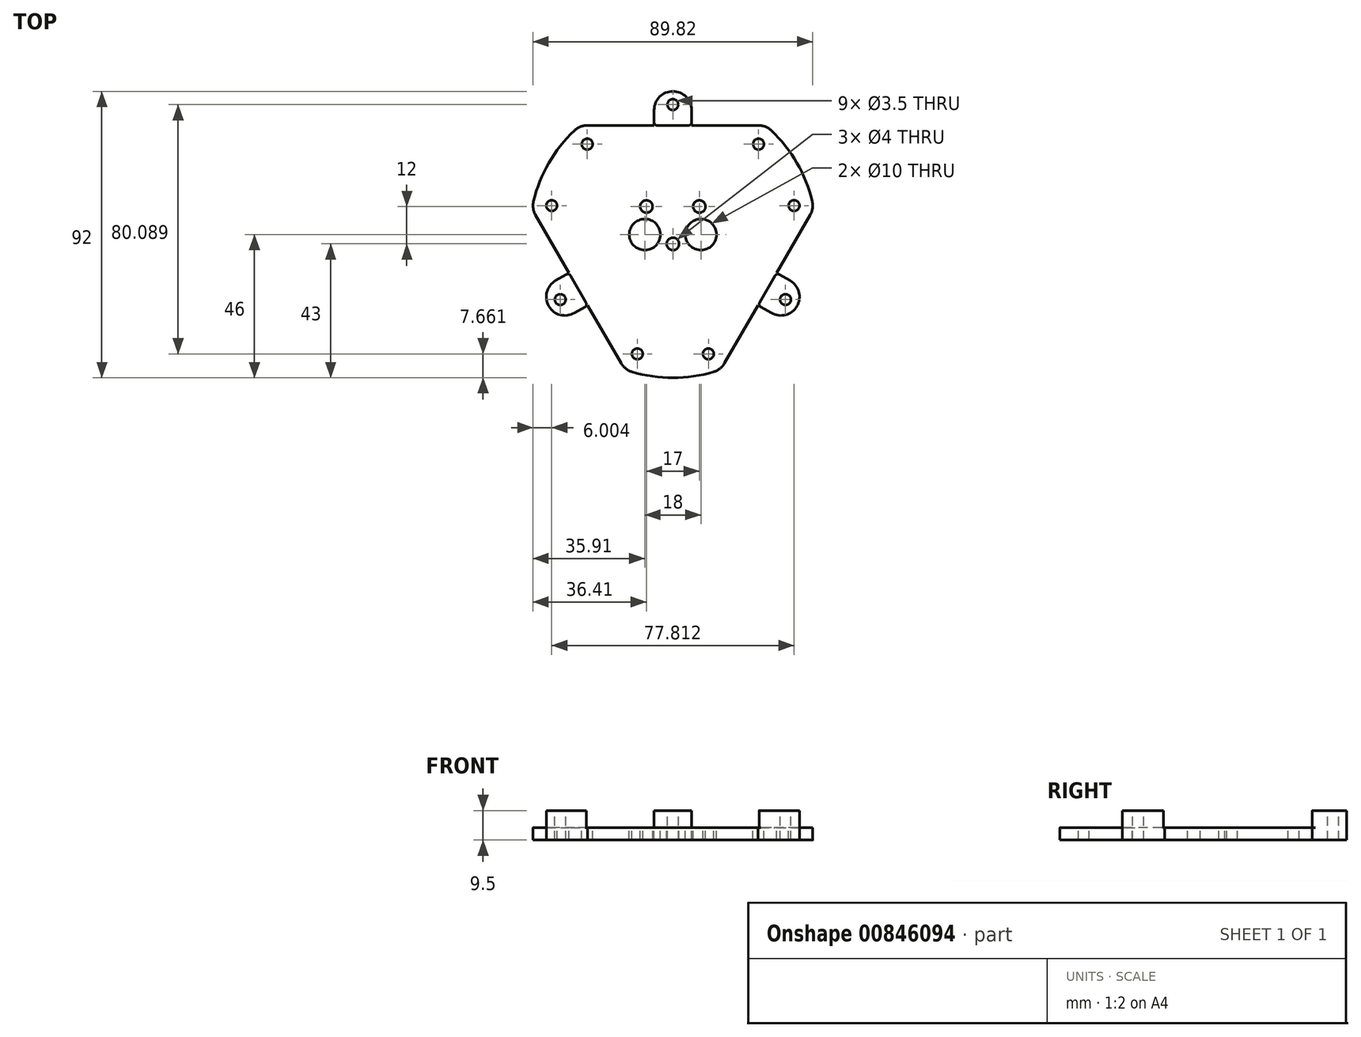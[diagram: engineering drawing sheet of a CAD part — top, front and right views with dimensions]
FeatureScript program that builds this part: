
annotation { "Feature Type Name" : "Feature", "Feature Type Description" : "" }
export const myFeature = defineFeature(function(context is Context, id is Id, definition is map)
    precondition{}
    {
        {
            var Q0;
            Q0=qCreatedBy(makeId("Top.planeOp"),FACE);
            var sketch = newSketch(context, id + "F0", { "sketchPlane" : qUnion([Q0])});
            skCircle(sketch, "E0", {"center": v(-38.9, 9.3) * mm, "radius": 1.75 * mm});
            skCircle(sketch, "E1", {"center": v(-38.9, 9.3) * mm, "radius": 6 * mm});
            skCircle(sketch, "E2", {"center": v(-11.4, -38.34) * mm, "radius": 1.75 * mm});
            skCircle(sketch, "E3", {"center": v(-11.4, -38.34) * mm, "radius": 6 * mm});
            skCircle(sketch, "E4", {"center": v(11.4, -38.34) * mm, "radius": 6 * mm});
            skCircle(sketch, "E5", {"center": v(11.4, -38.34) * mm, "radius": 1.75 * mm});
            skCircle(sketch, "E6", {"center": v(38.9, 9.3) * mm, "radius": 1.75 * mm});
            skCircle(sketch, "E7", {"center": v(38.9, 9.3) * mm, "radius": 6 * mm});
            skCircle(sketch, "E8", {"center": v(-27.5, 29.05) * mm, "radius": 1.75 * mm});
            skCircle(sketch, "E9", {"center": v(-27.5, 29.05) * mm, "radius": 6 * mm});
            skCircle(sketch, "E10", {"center": v(27.5, 29.05) * mm, "radius": 1.75 * mm});
            skCircle(sketch, "E11", {"center": v(27.5, 29.05) * mm, "radius": 6 * mm});
            skLineSegment(sketch, "E12", {"start": v(-27.5, 29.05) * mm, "end": v(27.5, 29.05) * mm, "construction": true});
            skLineSegment(sketch, "E13", {"start": v(38.9, 9.3) * mm, "end": v(11.4, -38.34) * mm, "construction": true});
            skLineSegment(sketch, "E14", {"start": v(-11.4, -38.34) * mm, "end": v(-38.9, 9.3) * mm, "construction": true});
            skCircle(sketch, "E15", {"center": v(0, 0) * mm, "radius": 40 * mm, "construction": true});
            skCircle(sketch, "E16", {"center": v(0, 0) * mm, "radius": 46 * mm});
            skLineSegment(sketch, "E17", {"start": v(-44.1, 6.3) * mm, "end": v(-16.6, -41.34) * mm});
            skLineSegment(sketch, "E18", {"start": v(16.6, -41.34) * mm, "end": v(44.1, 6.3) * mm});
            skLineSegment(sketch, "E19", {"start": v(27.5, 35.05) * mm, "end": v(-27.5, 35.05) * mm});
            skLineSegment(sketch, "E20", {"start": v(-20, 0) * mm, "end": v(20, 0) * mm, "construction": true});
            skLineSegment(sketch, "E21", {"start": v(0, 20) * mm, "end": v(0, -20) * mm, "construction": true});
            skCircle(sketch, "E22", {"center": v(-9, 0) * mm, "radius": 5 * mm});
            skCircle(sketch, "E23", {"center": v(9, 0) * mm, "radius": 5 * mm});
            skLineSegment(sketch, "E24.bottom", {"start": v(-15, -6) * mm, "end": v(15, -6) * mm});
            skLineSegment(sketch, "E24.top", {"start": v(-15, 12) * mm, "end": v(15, 12) * mm});
            skLineSegment(sketch, "E24.left", {"start": v(-15, -6) * mm, "end": v(-15, 12) * mm});
            skLineSegment(sketch, "E24.right", {"start": v(15, -6) * mm, "end": v(15, 12) * mm});
            skPoint(sketch, "E25", {"position": v(0, -6) * mm});
            skCircle(sketch, "E26", {"center": v(0, -3) * mm, "radius": 2 * mm});
            skCircle(sketch, "E27", {"center": v(-8.5, 9) * mm, "radius": 2 * mm});
            skCircle(sketch, "E28", {"center": v(8.5, 9) * mm, "radius": 2 * mm});
            skLineSegment(sketch, "E29", {"start": v(0, 0) * mm, "end": v(-30.35, -17.52) * mm, "construction": true});
            skLineSegment(sketch, "E30", {"start": v(0, 0) * mm, "end": v(30.35, -17.52) * mm, "construction": true});
            skLineSegment(sketch, "E31", {"start": v(0, 0) * mm, "end": v(0, 40) * mm, "construction": true});
            skLineSegment(sketch, "E32", {"start": v(-30.35, -17.52) * mm, "end": v(-34.64, -20) * mm, "construction": true});
            skLineSegment(sketch, "E33", {"start": v(30.35, -17.52) * mm, "end": v(34.64, -20) * mm, "construction": true});
            skArc(sketch, "E34", {"start": v(5.98, 39.55) * mm, "mid": v(0, 46) * mm, "end": v(-5.98, 39.55) * mm});
            skArc(sketch, "E35", {"start": v(31.26, -24.96) * mm, "mid": v(39.84, -23) * mm, "end": v(37.24, -14.6) * mm});
            skArc(sketch, "E36", {"start": v(-37.24, -14.6) * mm, "mid": v(-39.84, -23) * mm, "end": v(-31.26, -24.96) * mm});
            skLineSegment(sketch, "E37", {"start": v(-34.64, -20) * mm, "end": v(-39.84, -23) * mm, "construction": true});
            skLineSegment(sketch, "E38", {"start": v(0, 40) * mm, "end": v(0, 46) * mm, "construction": true});
            skLineSegment(sketch, "E39", {"start": v(34.64, -20) * mm, "end": v(39.84, -23) * mm, "construction": true});
            skLineSegment(sketch, "E40", {"start": v(6, 40) * mm, "end": v(6, 35.05) * mm});
            skLineSegment(sketch, "E41", {"start": v(-6, 40) * mm, "end": v(-6, 35.05) * mm});
            skPoint(sketch, "E41.endSnap0", {"position": v(0, 35.05) * mm});
            skCircle(sketch, "E42", {"center": v(0, 41.75) * mm, "radius": 1.75 * mm});
            skLineSegment(sketch, "E43", {"start": v(-31.64, -25.2) * mm, "end": v(-27.35, -22.72) * mm});
            skLineSegment(sketch, "E44", {"start": v(-37.64, -14.8) * mm, "end": v(-33.35, -12.33) * mm});
            skLineSegment(sketch, "E45", {"start": v(31.64, -25.2) * mm, "end": v(27.35, -22.72) * mm});
            skLineSegment(sketch, "E46", {"start": v(37.64, -14.8) * mm, "end": v(33.35, -12.33) * mm});
            skCircle(sketch, "E47", {"center": v(-36.16, -20.88) * mm, "radius": 1.75 * mm});
            skCircle(sketch, "E48", {"center": v(36.16, -20.87) * mm, "radius": 1.75 * mm});
            skSolve(sketch);
        }
        {
            var Q0;
            Q0=makeQuery(id+"F0.imprint","IMPRINT",FACE,{"disambiguationData":[TD([[makeQuery(id+"F0.imprint","IMPRINT",EDGE,{"derivedFrom":sQuery(id+"F0.wireOp",EDGE,"pkLgbIjD-KCy6-X6lN-DSC3-kkQGYhp8DZLm")}),-1.0]])]});
            var Q1;
            {var subQ0=sQuery(id+"F0.wireOp",EDGE,"E17");Q1=makeQuery(id+"F0.imprint","IMPRINT",FACE,{"disambiguationData":[TD([[makeQuery(id+"F0.imprint","IMPRINT",EDGE,{"derivedFrom":subQ0}),1.0]])]});}
            var Q2;
            Q2=makeQuery(id+"F0.imprint","IMPRINT",FACE,{"disambiguationData":[TD([[makeQuery(id+"F0.imprint","IMPRINT",EDGE,{"derivedFrom":sQuery(id+"F0.wireOp",EDGE,"E0")}),-1.0]])]});
            var Q3;
            Q3=makeQuery(id+"F0.imprint","IMPRINT",FACE,{"disambiguationData":[TD([[makeQuery(id+"F0.imprint","IMPRINT",EDGE,{"derivedFrom":sQuery(id+"F0.wireOp",EDGE,"E8")}),-1.0]])]});
            var Q4;
            {var subQ0=sQuery(id+"F0.wireOp",EDGE,"E19");Q4=makeQuery(id+"F0.imprint","IMPRINT",FACE,{"disambiguationData":[TD([[makeQuery(id+"F0.imprint","IMPRINT",EDGE,{"derivedFrom":subQ0}),1.0]])]});}
            var Q5;
            Q5=makeQuery(id+"F0.imprint","IMPRINT",FACE,{"disambiguationData":[TD([[makeQuery(id+"F0.imprint","IMPRINT",EDGE,{"derivedFrom":sQuery(id+"F0.wireOp",EDGE,"E10")}),-1.0]])]});
            var Q6;
            Q6=makeQuery(id+"F0.imprint","IMPRINT",FACE,{"disambiguationData":[TD([[makeQuery(id+"F0.imprint","IMPRINT",EDGE,{"derivedFrom":sQuery(id+"F0.wireOp",EDGE,"E6")}),-1.0]])]});
            var Q7;
            Q7=makeQuery(id+"F0.imprint","IMPRINT",FACE,{"disambiguationData":[TD([[makeQuery(id+"F0.imprint","IMPRINT",EDGE,{"derivedFrom":sQuery(id+"F0.wireOp",EDGE,"E5")}),-1.0]])]});
            var Q8;
            Q8=makeQuery(id+"F0.imprint","IMPRINT",FACE,{"disambiguationData":[TD([[makeQuery(id+"F0.imprint","IMPRINT",EDGE,{"derivedFrom":sQuery(id+"F0.wireOp",EDGE,"E2")}),-1.0]])]});
            var Q9;
            Q9=makeQuery(id+"F0.imprint","IMPRINT",FACE,{"disambiguationData":[TD([[makeQuery(id+"F0.imprint","IMPRINT",EDGE,{"derivedFrom":sQuery(id+"F0.wireOp",EDGE,"swXuQqJx-4WA5-xotS-5m6w-y178Cp15UTXd")}),-1.0]])]});
            var Q10;
            Q10=makeQuery(id+"F0.imprint","IMPRINT",FACE,{"disambiguationData":[TD([[makeQuery(id+"F0.imprint","IMPRINT",EDGE,{"derivedFrom":sQuery(id+"F0.wireOp",EDGE,"OkQYxNT0-b6hR-lTen-oeqQ-3yULjjXIIMOo")}),-1.0]])]});
            var Q11;
            {var subQ17=sQuery(id+"F0.wireOp",EDGE,"E18");Q11=makeQuery(id+"F0.imprint","IMPRINT",FACE,{"disambiguationData":[TD([[makeQuery(id+"F0.imprint","IMPRINT",EDGE,{"derivedFrom":subQ17}),1.0]])]});}
            var Q12;
            Q12=makeQuery(id+"F0.imprint","IMPRINT",FACE,{"disambiguationData":[TD([[makeQuery(id+"F0.imprint","IMPRINT",EDGE,{"derivedFrom":sQuery(id+"F0.wireOp",EDGE,"E22")}),-1.0]])]});
            var Q13;
            Q13=makeQuery(id+"F0.imprint","IMPRINT",FACE,{"disambiguationData":[TD([[makeQuery(id+"F0.imprint","IMPRINT",EDGE,{"derivedFrom":sQuery(id+"F0.wireOp",EDGE,"E24.bottom")}),-1.0]])]});
            var Q14;
            {var subQ0=sQuery(id+"F0.wireOp",EDGE,"E40");Q14=makeQuery(id+"F0.imprint","IMPRINT",FACE,{"disambiguationData":[TD([[makeQuery(id+"F0.imprint","IMPRINT",EDGE,{"derivedFrom":subQ0}),-1.0]])]});}
            var Q15;
            {var subQ0=sQuery(id+"F0.wireOp",EDGE,"E43");Q15=makeQuery(id+"F0.imprint","IMPRINT",FACE,{"disambiguationData":[TD([[makeQuery(id+"F0.imprint","IMPRINT",EDGE,{"derivedFrom":subQ0}),1.0]])]});}
            var Q16;
            {var subQ3=sQuery(id+"F0.wireOp",EDGE,"E45");Q16=makeQuery(id+"F0.imprint","IMPRINT",FACE,{"disambiguationData":[TD([[makeQuery(id+"F0.imprint","IMPRINT",EDGE,{"derivedFrom":subQ3}),-1.0]])]});}
            extrude(context, id + "F1", {"entities" : qUnion([Q0, Q1, Q2, Q3, Q4, Q5, Q6, Q7, Q8, Q9, Q10, Q11, Q12, Q13, Q14, Q15, Q16]), "oppositeDirection" : true, "depth" : 4 * mm, "offsetDistance" : 25 * mm});
        }
        {
            var Q0;
            {var subQ0=sQuery(id+"F0.wireOp",EDGE,"E43");Q0=makeQuery(id+"F0.imprint","IMPRINT",FACE,{"disambiguationData":[TD([[makeQuery(id+"F0.imprint","IMPRINT",EDGE,{"derivedFrom":subQ0}),1.0]])]});}
            var Q1;
            {var subQ0=sQuery(id+"F0.wireOp",EDGE,"E40");Q1=makeQuery(id+"F0.imprint","IMPRINT",FACE,{"disambiguationData":[TD([[makeQuery(id+"F0.imprint","IMPRINT",EDGE,{"derivedFrom":subQ0}),-1.0]])]});}
            var Q2;
            {var subQ3=sQuery(id+"F0.wireOp",EDGE,"E45");Q2=makeQuery(id+"F0.imprint","IMPRINT",FACE,{"disambiguationData":[TD([[makeQuery(id+"F0.imprint","IMPRINT",EDGE,{"derivedFrom":subQ3}),-1.0]])]});}
            extrude(context, id + "F2", {"entities" : qUnion([Q0, Q1, Q2]), "operationType" : NewBodyOperationType.ADD, "depth" : 5.5 * mm, "offsetDistance" : 25 * mm});
        }
        {
            var Q0;
            Q0=makeQuery(id+"F2.opExtrude","SWEPT_EDGE",EDGE,{"disambiguationData":[OSD([sQuery(id+"F0.wireOp",EDGE,"E19"),sQuery(id+"F0.wireOp",EDGE,"E40")])]});
            var Q1;
            Q1=makeQuery(id+"F2.opExtrude","SWEPT_EDGE",EDGE,{"disambiguationData":[OSD([sQuery(id+"F0.wireOp",EDGE,"E19"),sQuery(id+"F0.wireOp",EDGE,"E41")])]});
            var Q2;
            Q2=makeQuery(id+"F2.opExtrude","SWEPT_EDGE",EDGE,{"disambiguationData":[OSD([sQuery(id+"F0.wireOp",EDGE,"E18"),sQuery(id+"F0.wireOp",EDGE,"E46")])]});
            var Q3;
            Q3=makeQuery(id+"F2.opExtrude","SWEPT_EDGE",EDGE,{"disambiguationData":[OSD([sQuery(id+"F0.wireOp",EDGE,"E18"),sQuery(id+"F0.wireOp",EDGE,"E45")])]});
            var Q4;
            Q4=makeQuery(id+"F2.opExtrude","SWEPT_EDGE",EDGE,{"disambiguationData":[OSD([sQuery(id+"F0.wireOp",EDGE,"E17"),sQuery(id+"F0.wireOp",EDGE,"E44")])]});
            var Q5;
            Q5=makeQuery(id+"F2.opExtrude","SWEPT_EDGE",EDGE,{"disambiguationData":[OSD([sQuery(id+"F0.wireOp",EDGE,"E17"),sQuery(id+"F0.wireOp",EDGE,"E43")])]});
            fillet(context, id + "F3", {"entities" : qUnion([Q0, Q1, Q2, Q3, Q4, Q5]), "radius" : 1 * mm, "tangentPropagation" : true, "allowEdgeOverflow" : false});
        }
    });
